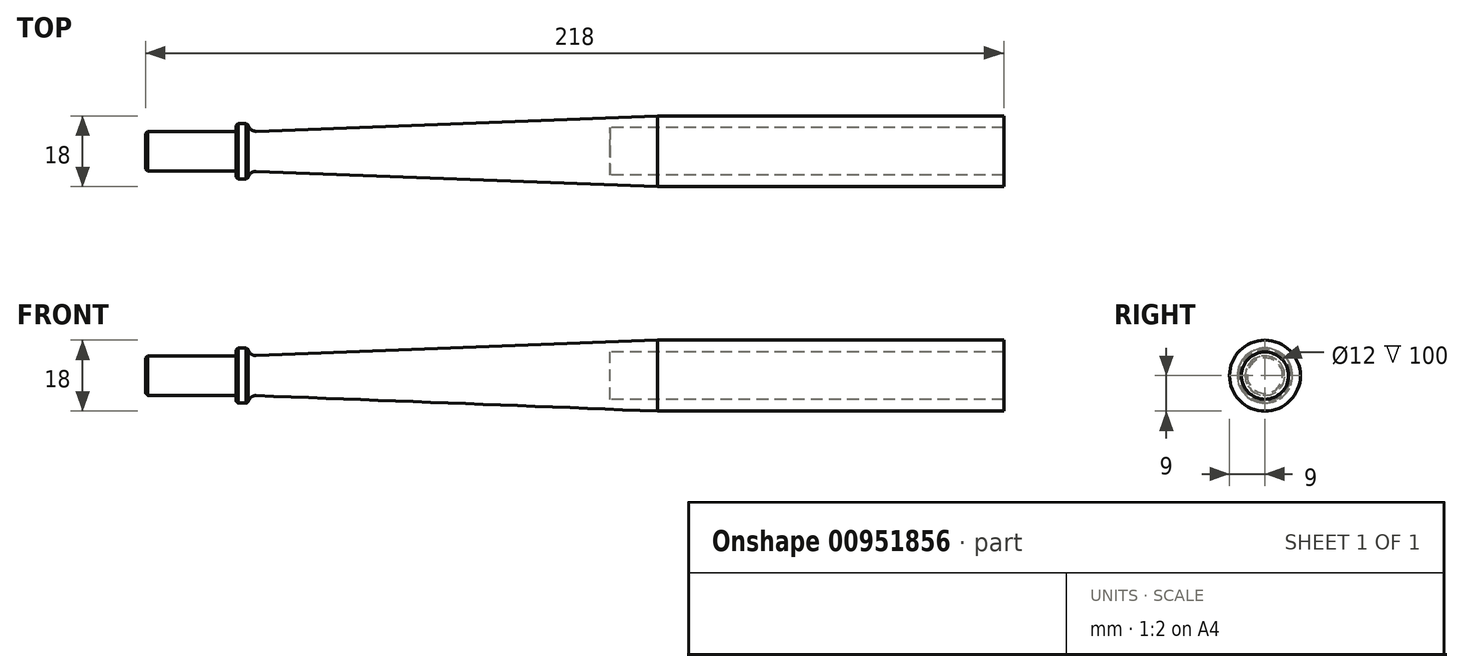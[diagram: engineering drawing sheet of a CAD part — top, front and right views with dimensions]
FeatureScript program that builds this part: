
annotation { "Feature Type Name" : "Feature", "Feature Type Description" : "" }
export const myFeature = defineFeature(function(context is Context, id is Id, definition is map)
    precondition{}
    {
        {
            var Q0;
            Q0=qCreatedBy(makeId("Front.planeOp"),FACE);
            var sketch = newSketch(context, id + "F0", { "sketchPlane" : qUnion([Q0])});
            skLineSegment(sketch, "E0", {"start": v(0, 0) * mm, "end": v(0, 5) * mm});
            skLineSegment(sketch, "E1", {"start": v(0, 5) * mm, "end": v(23, 5) * mm});
            skLineSegment(sketch, "E2", {"start": v(23, 5) * mm, "end": v(23, 7) * mm});
            skLineSegment(sketch, "E3", {"start": v(23, 7) * mm, "end": v(26, 7) * mm});
            skLineSegment(sketch, "E4", {"start": v(26, 7) * mm, "end": v(26, 5) * mm});
            skLineSegment(sketch, "E5", {"start": v(218, 0) * mm, "end": v(0, 0) * mm});
            skLineSegment(sketch, "E6", {"start": v(218, 0) * mm, "end": v(218, 9) * mm});
            skLineSegment(sketch, "E7", {"start": v(218, 9) * mm, "end": v(130, 9) * mm});
            skLineSegment(sketch, "E8", {"start": v(130, 9) * mm, "end": v(26, 5) * mm});
            skSolve(sketch);
        }
        {
            var Q0;
            Q0=makeQuery(id+"F0.imprint","IMPRINT",FACE,{"disambiguationData":[TD([[makeQuery(id+"F0.imprint","IMPRINT",EDGE,{"derivedFrom":sQuery(id+"F0.wireOp",EDGE,"E0")}),-1.0]])]});
            var Q1;
            Q1=sQuery(id+"F0.wireOp",EDGE,"E5");
            revolve(context, id + "F1", {"surfaceOperationType" : NewSurfaceOperationType.NEW, "entities" : qUnion([Q0]), "axis" : qUnion([Q1]), "revolveType" : RevolveType.FULL});
        }
        {
            var Q0;
            Q0=makeQuery(id+"F1.opRevolve","SWEPT_EDGE",EDGE,{"disambiguationData":[OSD([sQuery(id+"F0.wireOp",EDGE,"E4"),sQuery(id+"F0.wireOp",EDGE,"E8")])]});
            fillet(context, id + "F2", {"entities" : qUnion([Q0]), "radius" : 2 * mm, "tangentPropagation" : true, "allowEdgeOverflow" : false});
        }
        {
            var Q0;
            Q0=makeQuery(id+"F1.opRevolve","SWEPT_EDGE",EDGE,{"disambiguationData":[OSD([sQuery(id+"F0.wireOp",EDGE,"E2"),sQuery(id+"F0.wireOp",EDGE,"E3")])]});
            var Q1;
            Q1=makeQuery(id+"F2.opFillet","BLEND_EDGE",EDGE,{"blendedFrom":[makeQuery(id+"F1.opRevolve","SWEPT_EDGE",EDGE,{"disambiguationData":[OSD([sQuery(id+"F0.wireOp",EDGE,"E4"),sQuery(id+"F0.wireOp",EDGE,"3qa7xNLN-yixq-rNpI-Rn1v-gfBrvUUDBYIc")])]}),makeQuery(id+"F1.opRevolve","SWEPT_FACE",FACE,{"disambiguationData":[OSD([sQuery(id+"F0.wireOp",EDGE,"E3")])]})],"blendedInto":[makeQuery(id+"F1.opRevolve","SWEPT_FACE",FACE,{"disambiguationData":[OSD([sQuery(id+"F0.wireOp",EDGE,"E3")])]})]});
            var Q2;
            Q2=makeQuery(id+"F1.opRevolve","SWEPT_EDGE",EDGE,{"disambiguationData":[OSD([sQuery(id+"F0.wireOp",EDGE,"E0"),sQuery(id+"F0.wireOp",EDGE,"E1")])]});
            chamfer(context, id + "F3", {"entities" : qUnion([Q0, Q1, Q2]), "width" : .5 * mm, "tangentPropagation" : true});
        }
        {
            var Q0;
            Q0=qCreatedBy(makeId("Right.planeOp"),FACE);
            var sketch = newSketch(context, id + "F4", { "sketchPlane" : qUnion([Q0])});
            skCircle(sketch, "E9", {"center": v(0, 0) * mm, "radius": 6 * mm});
            skSolve(sketch);
        }
        {
            var Q0;
            Q0 = qSketchRegion(id + "F4", true);
            extrude(context, id + "F5", {"entities" : qUnion([Q0]), "operationType" : NewBodyOperationType.REMOVE, "depth" : 220 * mm, "hasOffset" : true, "offsetDistance" : 25 * mm, "hasSecondDirection" : true, "secondDirectionOppositeDirection" : false, "secondDirectionDepth" : 118 * mm});
        }
    });
